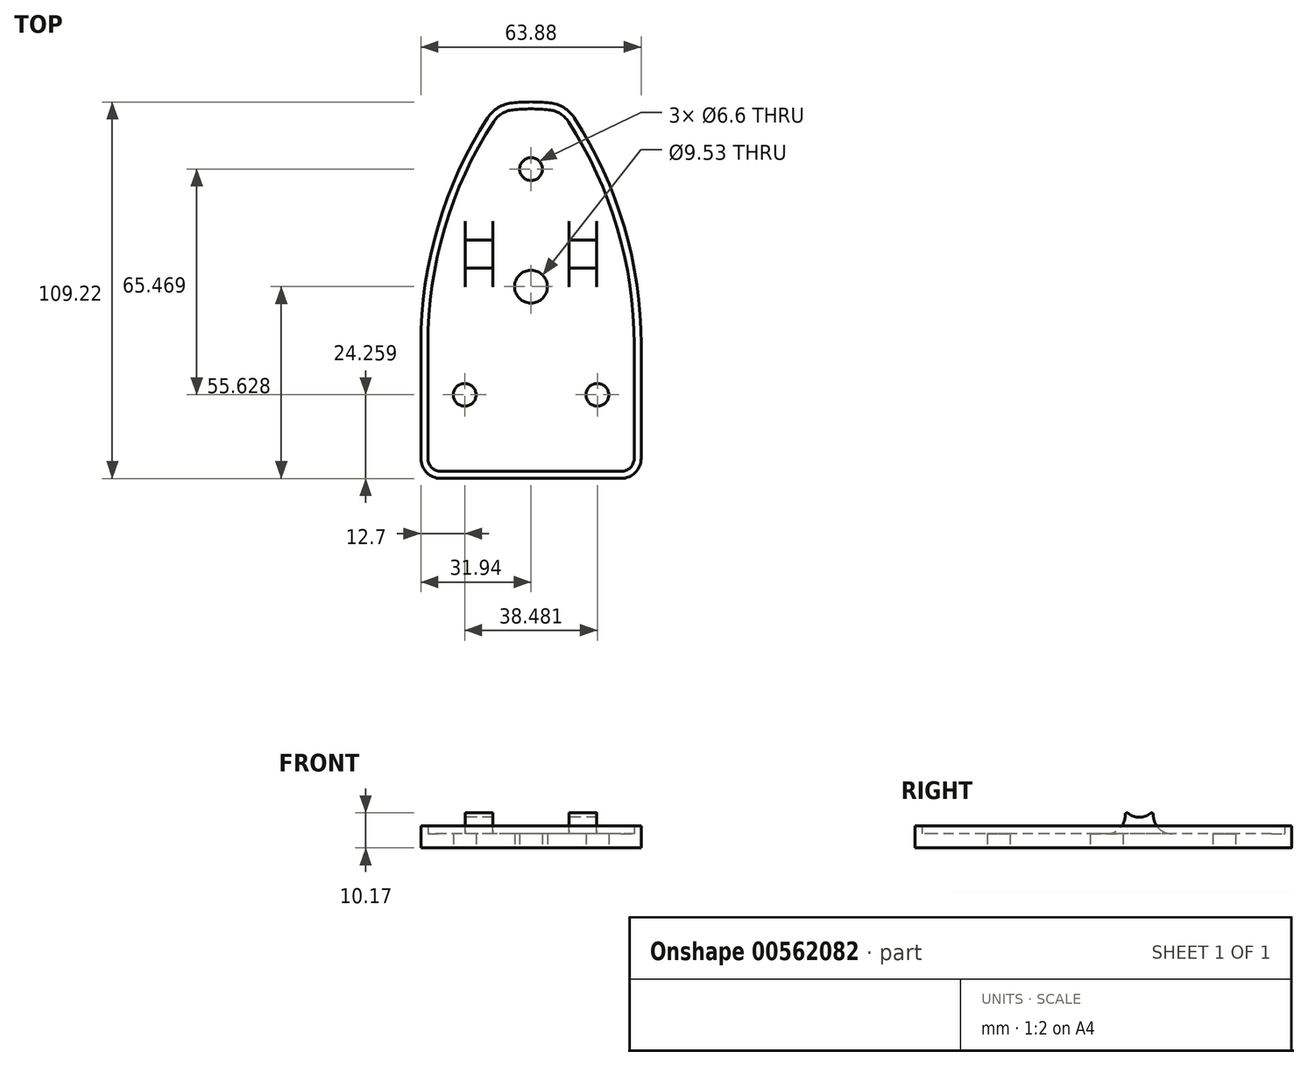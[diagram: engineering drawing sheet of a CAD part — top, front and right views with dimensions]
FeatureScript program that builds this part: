
annotation { "Feature Type Name" : "Feature", "Feature Type Description" : "" }
export const myFeature = defineFeature(function(context is Context, id is Id, definition is map)
    precondition{}
    {
        {
            var Q0;
            Q0=qCreatedBy(makeId("Top.planeOp"),FACE);
            var sketch = newSketch(context, id + "F0", { "sketchPlane" : qUnion([Q0])});
            skPoint(sketch, "E0", {"position": v(0, 0) * mm});
            skLineSegment(sketch, "E1", {"start": v(0, -105.16) * mm, "end": v(0, 0) * mm, "construction": true});
            skLineSegment(sketch, "E2", {"start": v(-29.9, -68.33) * mm, "end": v(-29.9, -101.35) * mm});
            skLineSegment(sketch, "E3", {"start": v(0, -105.16) * mm, "end": v(-26.1, -105.16) * mm});
            skArc(sketch, "E4.filletArc", {"start": v(-29.9, -101.35) * mm, "mid": v(-28.8, -104.04) * mm, "end": v(-26.1, -105.16) * mm});
            skArc(sketch, "E5", {"start": v(0, 0) * mm, "mid": v(-2.61, -0.07) * mm, "end": v(-5.22, -0.26) * mm});
            skArc(sketch, "E6", {"start": v(-10.86, -3.7) * mm, "mid": v(-25.05, -34.64) * mm, "end": v(-29.9, -68.33) * mm});
            skPoint(sketch, "E7.visualSharp", {"position": v(-8.9, -0.76) * mm});
            skArc(sketch, "E7.filletArc", {"start": v(-5.22, -0.26) * mm, "mid": v(-8.43, -1.34) * mm, "end": v(-10.86, -3.7) * mm});
            skArc(sketch, "E8.MirrorCS", {"start": v(0, 0) * mm, "mid": v(2.61, -0.07) * mm, "end": v(5.22, -0.26) * mm});
            skArc(sketch, "E9.MirrorCS", {"start": v(5.22, -0.26) * mm, "mid": v(8.43, -1.34) * mm, "end": v(10.86, -3.7) * mm});
            skArc(sketch, "E10.MirrorCS", {"start": v(10.86, -3.7) * mm, "mid": v(25.05, -34.64) * mm, "end": v(29.9, -68.33) * mm});
            skLineSegment(sketch, "E11.MirrorCS", {"start": v(29.9, -68.33) * mm, "end": v(29.9, -101.35) * mm});
            skArc(sketch, "E12.MirrorCS", {"start": v(29.9, -101.35) * mm, "mid": v(28.8, -104.04) * mm, "end": v(26.1, -105.16) * mm});
            skLineSegment(sketch, "E13.MirrorCS", {"start": v(0, -105.16) * mm, "end": v(26.1, -105.16) * mm});
            skCircle(sketch, "E14", {"center": v(0, -17.46) * mm, "radius": 3.3 * mm});
            skCircle(sketch, "E15", {"center": v(0, -51.56) * mm, "radius": 4.76 * mm});
            skCircle(sketch, "E16", {"center": v(-19.24, -82.93) * mm, "radius": 3.3 * mm});
            skCircle(sketch, "E17", {"center": v(19.24, -82.93) * mm, "radius": 3.3 * mm});
            skPoint(sketch, "E18", {"position": v(0, -46.8) * mm});
            skPoint(sketch, "E19", {"position": v(0, -20.76) * mm});
            skPoint(sketch, "E20", {"position": v(-22.54, -82.93) * mm});
            skPoint(sketch, "E21", {"position": v(-15.94, -82.93) * mm});
            skPoint(sketch, "E22", {"position": v(15.94, -82.93) * mm});
            skPoint(sketch, "E23", {"position": v(22.54, -82.93) * mm});
            skSolve(sketch);
        }
        {
            var Q0;
            Q0 = qSketchRegion(id + "F0", true);
            extrude(context, id + "F1", {"entities" : qUnion([Q0]), "depth" : 4.06 * mm, "offsetDistance" : 25.4 * mm});
        }
        {
            var Q0;
            Q0=qCreatedBy(makeId("Right.planeOp"),FACE);
            var sketch = newSketch(context, id + "F2", { "sketchPlane" : qUnion([Q0])});
            skPoint(sketch, "E24.0", {"position": v(0, 4.06) * mm});
            skPoint(sketch, "E25.0", {"position": v(0, 0) * mm});
            skLineSegment(sketch, "E26", {"start": v(-32.58, 4.06) * mm, "end": v(-51.63, 4.06) * mm});
            skArc(sketch, "E27", {"start": v(-37.66, 11.51) * mm, "mid": v(-42.1, 19.05) * mm, "end": v(-46.55, 11.51) * mm, "construction": true});
            skLineSegment(sketch, "E28", {"start": v(-42.1, 13.97) * mm, "end": v(-42.1, 19.05) * mm, "construction": true});
            skLineSegment(sketch, "E29", {"start": v(-42.1, 13.97) * mm, "end": v(-47.18, 13.97) * mm, "construction": true});
            skLineSegment(sketch, "E30.0", {"start": v(-20.76, 4.06) * mm, "end": v(-14.16, 4.06) * mm, "construction": true});
            skLineSegment(sketch, "E31", {"start": v(-42.1, 4.06) * mm, "end": v(-42.1, 13.97) * mm, "construction": true});
            skArc(sketch, "E32", {"start": v(-38.03, 9.65) * mm, "mid": v(-36.48, 5.7) * mm, "end": v(-32.58, 4.06) * mm});
            skArc(sketch, "E33", {"start": v(-51.63, 4.06) * mm, "mid": v(-47.72, 5.7) * mm, "end": v(-46.17, 9.65) * mm});
            skLineSegment(sketch, "E34", {"start": v(-37.66, 11.51) * mm, "end": v(-46.55, 11.51) * mm, "construction": true});
            skPoint(sketch, "E35", {"position": v(-42.1, 11.51) * mm});
            skLineSegment(sketch, "E36", {"start": v(-46.55, 11.51) * mm, "end": v(-46.55, 13.97) * mm, "construction": true});
            skLineSegment(sketch, "E37", {"start": v(-37.66, 11.51) * mm, "end": v(-37.66, 13.97) * mm, "construction": true});
            skArc(sketch, "E38", {"start": v(-45.34, 10.06) * mm, "mid": v(-42.1, 8.89) * mm, "end": v(-38.86, 10.06) * mm});
            skPoint(sketch, "E39.visualSharp", {"position": v(-37.66, 11.51) * mm});
            skArc(sketch, "E39.filletArc", {"start": v(-38.03, 9.65) * mm, "mid": v(-38.32, 10.12) * mm, "end": v(-38.86, 10.06) * mm});
            skPoint(sketch, "E40.visualSharp", {"position": v(-46.55, 11.51) * mm});
            skArc(sketch, "E40.filletArc", {"start": v(-45.34, 10.06) * mm, "mid": v(-45.89, 10.12) * mm, "end": v(-46.17, 9.65) * mm});
            skSolve(sketch);
        }
        {
            var Q0;
            Q0 = qSketchRegion(id + "F2", true);
            extrude(context, id + "F3", {"entities" : qUnion([Q0]), "operationType" : NewBodyOperationType.ADD, "depth" : 38.1 * mm, "offsetDistance" : 25.4 * mm, "symmetric" : true});
        }
        {
            var Q0;
            Q0 = qSketchRegion(id + "F2", true);
            extrude(context, id + "F4", {"entities" : qUnion([Q0]), "operationType" : NewBodyOperationType.REMOVE, "oppositeDirection" : true, "depth" : 22.17 * mm, "offsetDistance" : 25.4 * mm, "symmetric" : true});
        }
        {
            var Q0;
            Q0=qCreatedBy(makeId("Top.planeOp"),FACE);
            var sketch = newSketch(context, id + "F5", { "sketchPlane" : qUnion([Q0])});
            skArc(sketch, "E41.0", {"start": v(-10.86, -3.7) * mm, "mid": v(-25.05, -34.64) * mm, "end": v(-29.9, -68.33) * mm});
            skLineSegment(sketch, "E42.0", {"start": v(-29.9, -68.33) * mm, "end": v(-29.9, -101.35) * mm});
            skArc(sketch, "E43.0", {"start": v(29.9, -101.35) * mm, "mid": v(28.8, -104.04) * mm, "end": v(26.1, -105.16) * mm});
            skArc(sketch, "E44.0", {"start": v(-29.9, -101.35) * mm, "mid": v(-28.8, -104.04) * mm, "end": v(-26.1, -105.16) * mm});
            skLineSegment(sketch, "E45.0", {"start": v(26.1, -105.16) * mm, "end": v(-26.1, -105.16) * mm});
            skLineSegment(sketch, "E46.0", {"start": v(29.9, -68.33) * mm, "end": v(29.9, -101.35) * mm});
            skArc(sketch, "E47.0", {"start": v(10.86, -3.7) * mm, "mid": v(25.05, -34.64) * mm, "end": v(29.9, -68.33) * mm});
            skArc(sketch, "E48.0", {"start": v(-5.22, -0.26) * mm, "mid": v(-8.43, -1.34) * mm, "end": v(-10.86, -3.7) * mm});
            skArc(sketch, "E49.0", {"start": v(5.22, -0.26) * mm, "mid": v(8.43, -1.34) * mm, "end": v(10.86, -3.7) * mm});
            skArc(sketch, "E50.0", {"start": v(-5.22, -0.26) * mm, "mid": v(0, 0) * mm, "end": v(5.22, -0.26) * mm});
            skArc(sketch, "E51.0", {"start": v(-5.42, 1.76) * mm, "mid": v(0, 2.03) * mm, "end": v(5.42, 1.76) * mm});
            skArc(sketch, "E51.1", {"start": v(5.42, 1.76) * mm, "mid": v(9.49, 0.4) * mm, "end": v(12.56, -2.6) * mm});
            skArc(sketch, "E51.2", {"start": v(-5.42, 1.76) * mm, "mid": v(-9.49, 0.4) * mm, "end": v(-12.56, -2.6) * mm});
            skArc(sketch, "E51.3", {"start": v(12.56, -2.6) * mm, "mid": v(27, -34.07) * mm, "end": v(31.94, -68.33) * mm});
            skLineSegment(sketch, "E51.4", {"start": v(31.94, -68.33) * mm, "end": v(31.94, -101.35) * mm});
            skArc(sketch, "E51.5", {"start": v(31.94, -101.35) * mm, "mid": v(30.23, -105.48) * mm, "end": v(26.1, -107.19) * mm});
            skArc(sketch, "E51.6", {"start": v(-12.56, -2.6) * mm, "mid": v(-27, -34.07) * mm, "end": v(-31.94, -68.33) * mm});
            skLineSegment(sketch, "E51.7", {"start": v(-31.94, -68.33) * mm, "end": v(-31.94, -101.35) * mm});
            skArc(sketch, "E51.8", {"start": v(-31.94, -101.35) * mm, "mid": v(-30.23, -105.48) * mm, "end": v(-26.1, -107.19) * mm});
            skLineSegment(sketch, "E51.9", {"start": v(26.1, -107.19) * mm, "end": v(-26.1, -107.19) * mm});
            skSolve(sketch);
        }
        {
            var Q0;
            Q0 = qSketchRegion(id + "F5", true);
            extrude(context, id + "F6", {"entities" : qUnion([Q0]), "operationType" : NewBodyOperationType.ADD, "depth" : 6.35 * mm, "offsetDistance" : 25.4 * mm});
        }
    });
